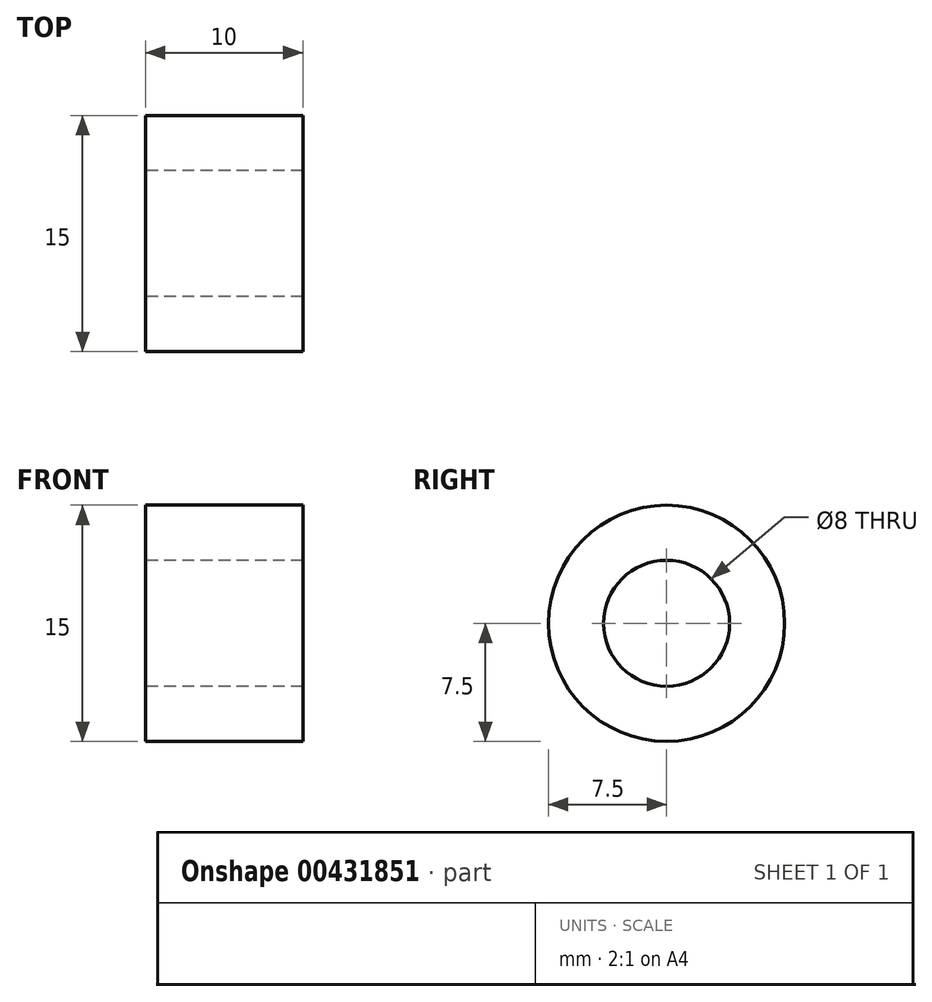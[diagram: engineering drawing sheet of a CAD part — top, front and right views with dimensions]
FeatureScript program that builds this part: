
annotation { "Feature Type Name" : "Feature", "Feature Type Description" : "" }
export const myFeature = defineFeature(function(context is Context, id is Id, definition is map)
    precondition{}
    {
        {
            var Q0;
            Q0=qCreatedBy(makeId("Right.planeOp"),FACE);
            var sketch = newSketch(context, id + "F0", { "sketchPlane" : qUnion([Q0])});
            skCircle(sketch, "E0", {"center": v(0, 0) * mm, "radius": 7.5 * mm});
            skSolve(sketch);
        }
        {
            var Q0;
            Q0 = qSketchRegion(id + "F0", true);
            extrude(context, id + "F1", {"entities" : qUnion([Q0]), "depth" : 10 * mm});
        }
        {
            var Q0;
            Q0=qCreatedBy(makeId("Right.planeOp"),FACE);
            var sketch = newSketch(context, id + "F2", { "sketchPlane" : qUnion([Q0])});
            skPoint(sketch, "E1", {"position": v(0, 0) * mm});
            skSolve(sketch);
        }
        {
            var Q0;
            Q0=sQuery(id+"F2.wireOp",VERTEX,"E1");
            var Q1;
            Q1=makeQuery(id+"F1.opExtrude","SWEPT_BODY",BODY,{"disambiguationData":[OSD([sQuery(id+"F0.wireOp",EDGE,"E0")])]});
            hole(context, id + "F3", {"style" : HoleStyle.SIMPLE, "endStyle" : HoleEndStyle.THROUGH, "oppositeDirection" : true, "holeDiameter" : 8 * mm, "isTappedThrough" : true, "tappedDepth" : 12 * mm, "tapClearance" : 3, "locations" : qUnion([Q0]), "scope" : qUnion([Q1])});
        }
    });
